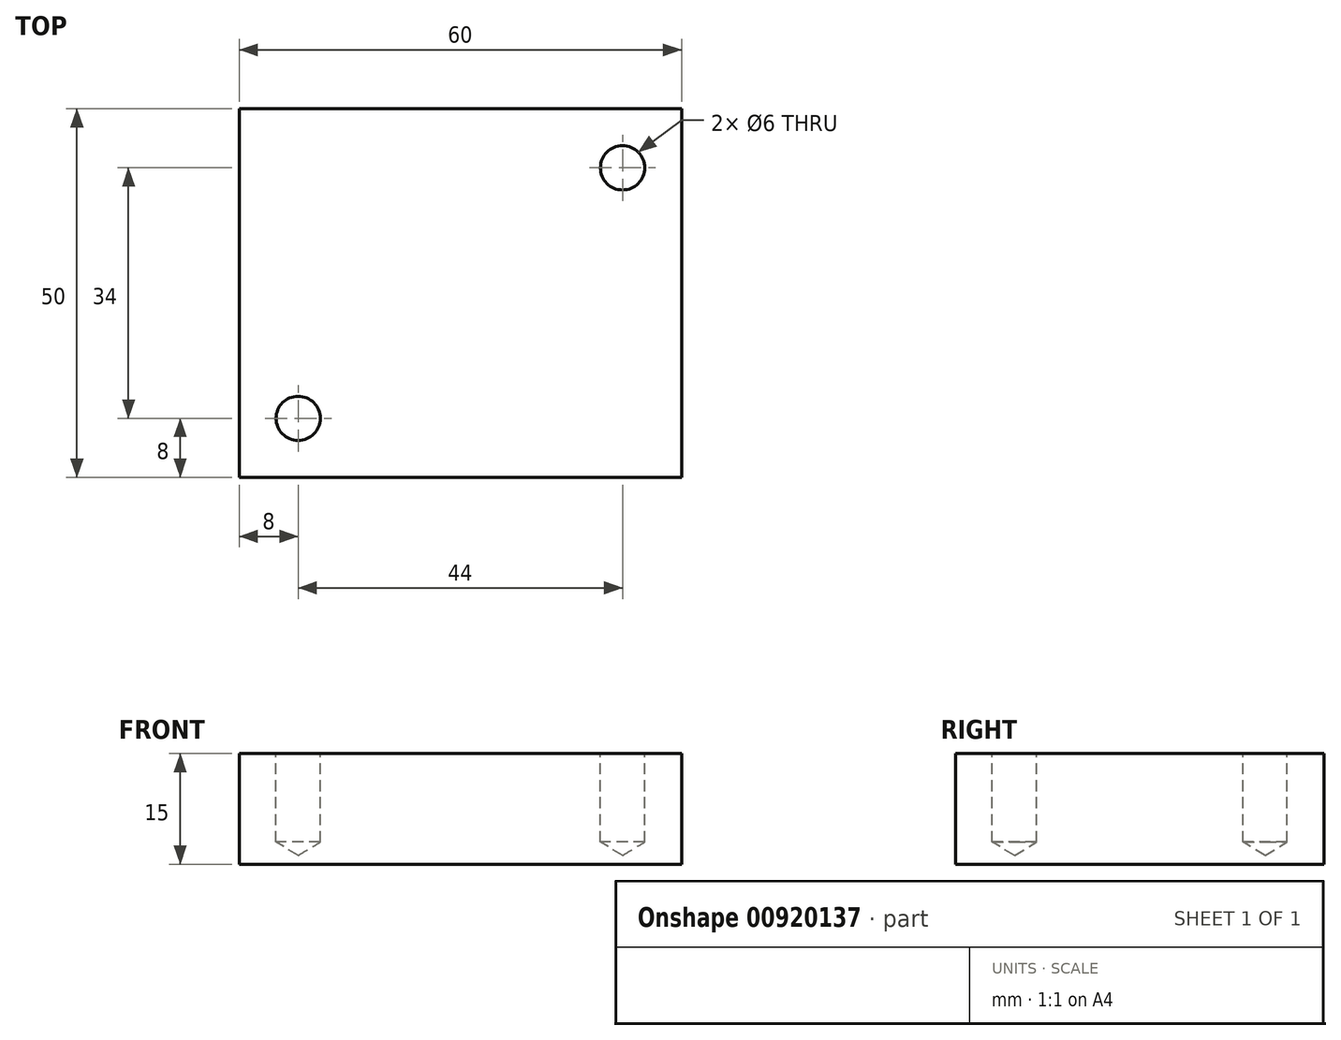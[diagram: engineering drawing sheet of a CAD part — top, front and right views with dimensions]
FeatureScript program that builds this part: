
annotation { "Feature Type Name" : "Feature", "Feature Type Description" : "" }
export const myFeature = defineFeature(function(context is Context, id is Id, definition is map)
    precondition{}
    {
        {
            var Q0;
            Q0=qCreatedBy(makeId("Top.planeOp"),FACE);
            var sketch = newSketch(context, id + "F0", { "sketchPlane" : qUnion([Q0])});
            skLineSegment(sketch, "E0.bottom", {"start": v(-30, -25) * mm, "end": v(30, -25) * mm});
            skLineSegment(sketch, "E0.top", {"start": v(-30, 25) * mm, "end": v(30, 25) * mm});
            skLineSegment(sketch, "E0.left", {"start": v(-30, -25) * mm, "end": v(-30, 25) * mm});
            skLineSegment(sketch, "E0.right", {"start": v(30, -25) * mm, "end": v(30, 25) * mm});
            skPoint(sketch, "E0.middle", {"position": v(0, 0) * mm});
            skSolve(sketch);
        }
        {
            var Q0;
            Q0 = qSketchRegion(id + "F0", true);
            extrude(context, id + "F1", {"entities" : qUnion([Q0]), "depth" : 15 * mm, "offsetDistance" : 25 * mm});
        }
        {
            var Q0;
            Q0=makeQuery(id+"F1.opExtrude","CAP_FACE",FACE,{"disambiguationData":[OSD([sQuery(id+"F0.wireOp",EDGE,"E0.bottom"),sQuery(id+"F0.wireOp",EDGE,"E0.top"),sQuery(id+"F0.wireOp",EDGE,"E0.left"),sQuery(id+"F0.wireOp",EDGE,"E0.right")])],"isStart":false});
            var sketch = newSketch(context, id + "F2", { "sketchPlane" : qUnion([Q0])});
            skLineSegment(sketch, "E1.bottom", {"start": v(-22, -17) * mm, "end": v(22, -17) * mm});
            skLineSegment(sketch, "E1.top", {"start": v(-22, 17) * mm, "end": v(22, 17) * mm});
            skLineSegment(sketch, "E1.left", {"start": v(-22, -17) * mm, "end": v(-22, 17) * mm});
            skLineSegment(sketch, "E1.right", {"start": v(22, -17) * mm, "end": v(22, 17) * mm});
            skPoint(sketch, "E1.middle", {"position": v(0, 0) * mm});
            skPoint(sketch, "E2", {"position": v(-22, -17) * mm});
            skPoint(sketch, "E3", {"position": v(22, 17) * mm});
            skPoint(sketch, "E4", {"position": v(-22, 17) * mm});
            skPoint(sketch, "E5", {"position": v(22, -17) * mm});
            skSolve(sketch);
        }
        {
            var Q0;
            Q0=sQuery(id+"F2.wireOp",VERTEX,"E2");
            var Q1;
            Q1=sQuery(id+"F2.wireOp",VERTEX,"E3");
            var Q2;
            Q2=makeQuery(id+"F1.opExtrude","SWEPT_BODY",BODY,{"disambiguationData":[OSD([sQuery(id+"F0.wireOp",EDGE,"E0.bottom"),sQuery(id+"F0.wireOp",EDGE,"E0.top"),sQuery(id+"F0.wireOp",EDGE,"E0.left"),sQuery(id+"F0.wireOp",EDGE,"E0.right")])]});
            hole(context, id + "F3", {"style" : HoleStyle.SIMPLE, "endStyle" : HoleEndStyle.BLIND, "standardTappedOrClearance" : lookupTablePath({ "standard" : "ISO", "size" : "6", "type" : "Drilled" }), "standardBlindInLast" : lookupTablePath({ "standard" : "ISO", "size" : "6", "type" : "Drilled" }), "holeDiameter" : 6 * mm, "majorDiameter" : 5 * mm, "holeDepth" : 12 * mm, "isTappedThrough" : true, "tappedDepth" : 12 * mm, "tapClearance" : 3, "locations" : qUnion([Q0, Q1]), "scope" : qUnion([Q2])});
        }
    });
